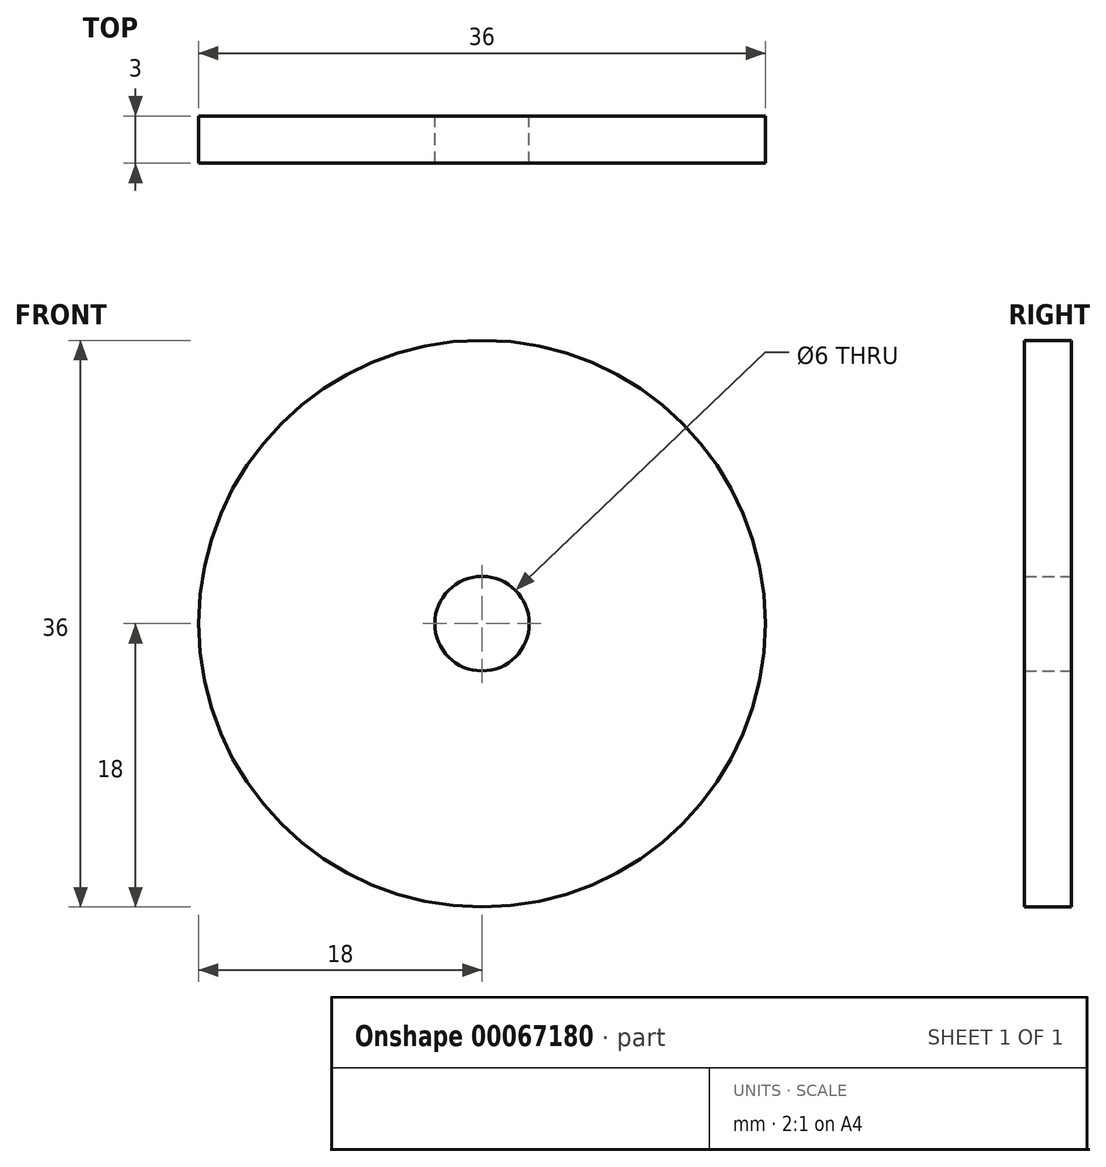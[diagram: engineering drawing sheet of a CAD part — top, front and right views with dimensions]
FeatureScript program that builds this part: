
annotation { "Feature Type Name" : "Feature", "Feature Type Description" : "" }
export const myFeature = defineFeature(function(context is Context, id is Id, definition is map)
    precondition{}
    {
        {
            var Q0;
            Q0=qCreatedBy(makeId("Front.planeOp"),FACE);
            var sketch = newSketch(context, id + "F0", { "sketchPlane" : qUnion([Q0])});
            skCircle(sketch, "E0", {"center": v(0, 0) * mm, "radius": 18 * mm});
            skCircle(sketch, "E1", {"center": v(0, 0) * mm, "radius": 3 * mm});
            skSolve(sketch);
        }
        {
            var Q0;
            Q0 = qSketchRegion(id + "F0", true);
            extrude(context, id + "F1", {"entities" : qUnion([Q0]), "depth" : 3 * mm});
        }
    });
